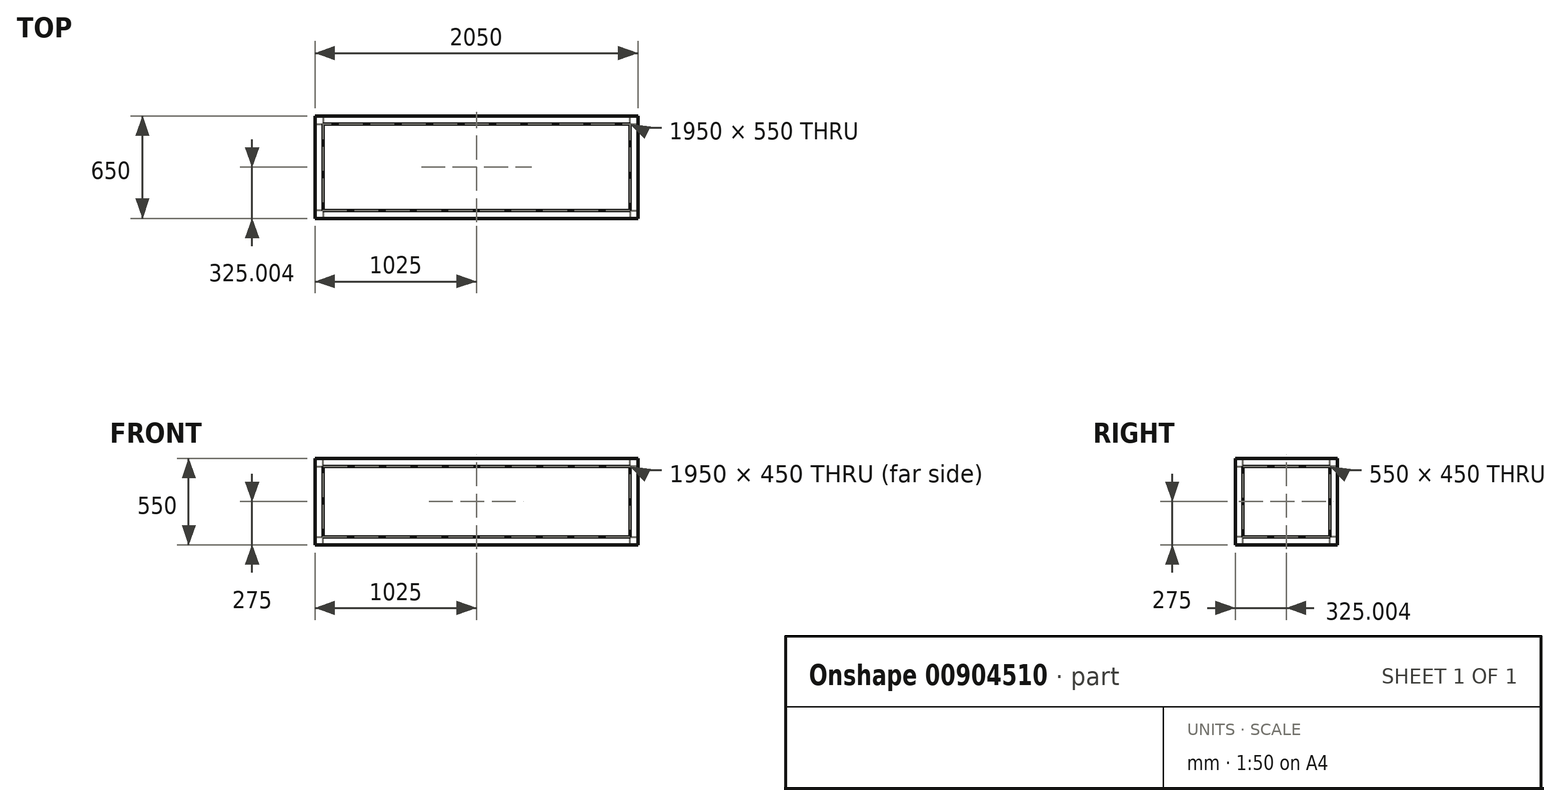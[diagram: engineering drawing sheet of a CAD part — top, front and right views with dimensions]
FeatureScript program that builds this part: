
annotation { "Feature Type Name" : "Feature", "Feature Type Description" : "" }
export const myFeature = defineFeature(function(context is Context, id is Id, definition is map)
    precondition{}
    {
        {
            var Q0;
            Q0=qCreatedBy(makeId("Top.planeOp"),FACE);
            var sketch = newSketch(context, id + "F0", { "sketchPlane" : qUnion([Q0])});
            skLineSegment(sketch, "E0.bottom", {"start": v(-969.08, 199.08) * mm, "end": v(1030.92, 199.08) * mm});
            skLineSegment(sketch, "E0.top", {"start": v(-969.08, -400.92) * mm, "end": v(1030.92, -400.92) * mm});
            skLineSegment(sketch, "E0.left", {"start": v(-969.08, 199.08) * mm, "end": v(-969.08, -400.92) * mm});
            skLineSegment(sketch, "E0.right", {"start": v(1030.92, 199.08) * mm, "end": v(1030.92, -400.92) * mm});
            skSolve(sketch);
        }
        {
            var Q0;
            Q0=qCreatedBy(makeId("Right.planeOp"),FACE);
            var sketch = newSketch(context, id + "F1", { "sketchPlane" : qUnion([Q0])});
            skLineSegment(sketch, "E1.bottom", {"start": v(174.08, -25) * mm, "end": v(224.08, -25) * mm});
            skLineSegment(sketch, "E1.top", {"start": v(174.08, 25) * mm, "end": v(224.08, 25) * mm});
            skLineSegment(sketch, "E1.left", {"start": v(174.08, -25) * mm, "end": v(174.08, 25) * mm});
            skLineSegment(sketch, "E1.right", {"start": v(224.08, -25) * mm, "end": v(224.08, 25) * mm});
            skPoint(sketch, "E1.middle", {"position": v(199.08, 0) * mm});
            skSolve(sketch);
        }
        {
            var Q0;
            Q0 = qSketchRegion(id + "F1", true);
            var Q1;
            Q1=sQuery(id+"F0.wireOp",EDGE,"E0.bottom");
            var Q2;
            Q2=sQuery(id+"F0.wireOp",EDGE,"E0.left");
            var Q3;
            Q3=sQuery(id+"F0.wireOp",EDGE,"E0.top");
            var Q4;
            Q4=sQuery(id+"F0.wireOp",EDGE,"E0.right");
            sweep(context, id + "F2", {"profiles" : qUnion([Q0]), "path" : qUnion([Q1, Q2, Q3, Q4])});
        }
        {
            var Q0;
            Q0=makeQuery(id+"F2.opSweep","SWEPT_BODY",BODY,{"disambiguationData":[OSD([sQuery(id+"F0.wireOp",EDGE,"E0.left"),sQuery(id+"F1.wireOp",EDGE,"E1.bottom"),sQuery(id+"F1.wireOp",EDGE,"E1.top"),sQuery(id+"F1.wireOp",EDGE,"E1.left"),sQuery(id+"F1.wireOp",EDGE,"E1.right")])]});
            transform(context, id + "F3", {"entities" : qUnion([Q0]), "transformType" : TransformType.TRANSLATION_3D, "dx" : 0 * mm, "dy" : 0 * mm, "dz" : 500 * mm, "makeCopy" : true});
        }
        {
            var Q0;
            Q0=makeQuery(id+"F2.opSweep","SWEPT_FACE",FACE,{"disambiguationData":[OSD([sQuery(id+"F0.wireOp",EDGE,"E0.right"),sQuery(id+"F1.wireOp",EDGE,"E1.top")])]});
            var sketch = newSketch(context, id + "F4", { "sketchPlane" : qUnion([Q0])});
            skLineSegment(sketch, "E2.bottom", {"start": v(-994.08, 224.08) * mm, "end": v(-944.08, 224.08) * mm});
            skLineSegment(sketch, "E2.top", {"start": v(-994.08, 174.08) * mm, "end": v(-944.08, 174.08) * mm});
            skLineSegment(sketch, "E2.left", {"start": v(-994.08, 224.08) * mm, "end": v(-994.08, 174.08) * mm});
            skLineSegment(sketch, "E2.right", {"start": v(-944.08, 224.08) * mm, "end": v(-944.08, 174.08) * mm});
            skLineSegment(sketch, "E3.bottom", {"start": v(-944.08, -375.92) * mm, "end": v(-994.08, -375.92) * mm});
            skLineSegment(sketch, "E3.top", {"start": v(-944.08, -425.92) * mm, "end": v(-994.08, -425.92) * mm});
            skLineSegment(sketch, "E3.left", {"start": v(-944.08, -375.92) * mm, "end": v(-944.08, -425.92) * mm});
            skLineSegment(sketch, "E3.right", {"start": v(-994.08, -375.92) * mm, "end": v(-994.08, -425.92) * mm});
            skLineSegment(sketch, "E4.bottom", {"start": v(1005.92, -375.92) * mm, "end": v(1055.92, -375.92) * mm});
            skLineSegment(sketch, "E4.top", {"start": v(1005.92, -425.92) * mm, "end": v(1055.92, -425.92) * mm});
            skLineSegment(sketch, "E4.left", {"start": v(1005.92, -375.92) * mm, "end": v(1005.92, -425.92) * mm});
            skLineSegment(sketch, "E4.right", {"start": v(1055.92, -375.92) * mm, "end": v(1055.92, -425.92) * mm});
            skLineSegment(sketch, "E5.bottom", {"start": v(1005.92, 174.08) * mm, "end": v(1055.92, 174.08) * mm});
            skLineSegment(sketch, "E5.top", {"start": v(1005.92, 224.08) * mm, "end": v(1055.92, 224.08) * mm});
            skLineSegment(sketch, "E5.left", {"start": v(1005.92, 174.08) * mm, "end": v(1005.92, 224.08) * mm});
            skLineSegment(sketch, "E5.right", {"start": v(1055.92, 174.08) * mm, "end": v(1055.92, 224.08) * mm});
            skSolve(sketch);
        }
        {
            var Q0;
            Q0 = qSketchRegion(id + "F4", true);
            extrude(context, id + "F5", {"entities" : qUnion([Q0]), "operationType" : NewBodyOperationType.ADD, "endBound" : BoundingType.UP_TO_NEXT, "depth" : 25 * mm, "offsetDistance" : 25 * mm});
        }
    });
